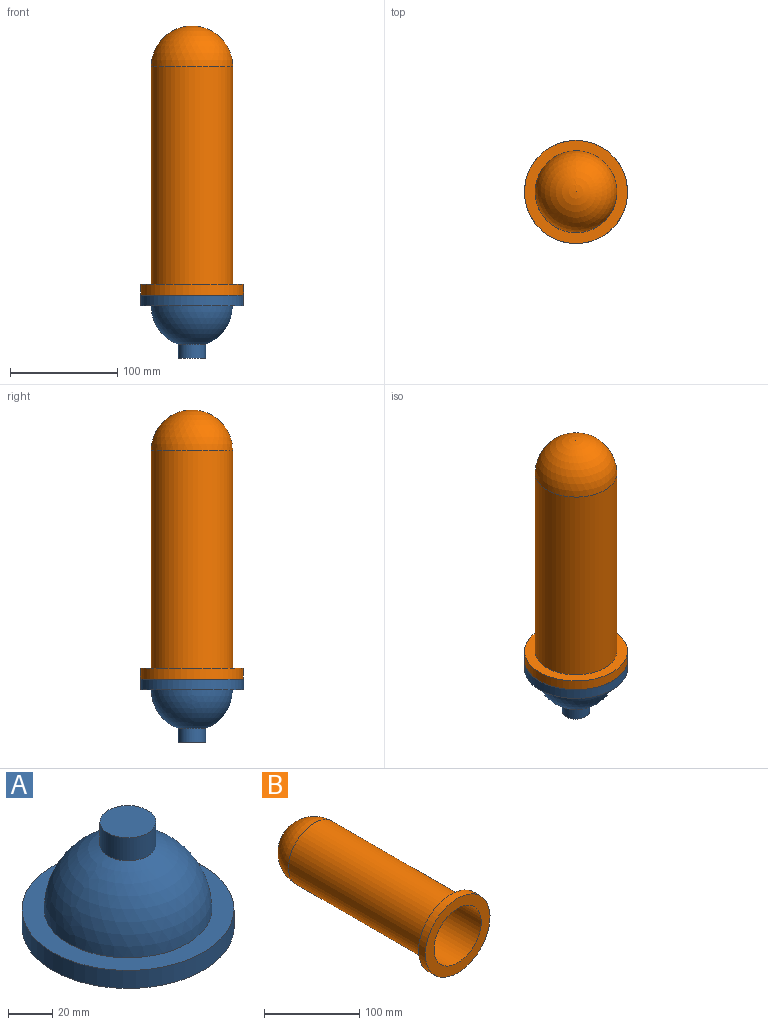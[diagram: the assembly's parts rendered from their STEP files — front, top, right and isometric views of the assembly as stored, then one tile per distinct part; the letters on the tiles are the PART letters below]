
ASSEMBLY  parts=2 mates=1
PART A: 8 faces, bbox 96.2x96.2x58.6 mm
  f0: sphere r=38.1mm, area 8599.1mm2, adj f2,f3
  f1: plane 25.4x25.4mm, normal (0,0,1), area 506.7mm2, adj f2
  f2: cylinder r=12.7mm len=25.4mm, axis (0,0,-1), area 1013.4mm2, adj f0,f1
  f3: plane 96.2x96.2mm, normal (0,0,1), area 2708.1mm2, adj f0,f4
  f4: cylinder r=48.1mm len=96.2mm, axis (0,0,1), area 3022.2mm2, adj f3,f6
  f5: cylinder r=35.1mm len=70.2mm, axis (0,0,1), area 2205.4mm2, adj f6,f7
  f6: plane 96.2x96.2mm, normal (0,0,-1), area 3397.9mm2, adj f4,f5
  f7: sphere r=35.1mm, area 7740.9mm2, adj f5
PART B: 7 faces, bbox 96.2x251.3x96.2 mm
  f0: cylinder r=35.1mm len=213.2mm, axis (0,1,0), area 47019.1mm2, adj f1,f3
  f1: sphere r=35.1mm, area 7740.9mm2, adj f0
  f2: cylinder r=48.1mm len=96.2mm, axis (0,1,0), area 3022.2mm2, adj f3,f4
  f3: plane 96.2x96.2mm, normal (0,-1,0), area 3397.9mm2, adj f0,f2
  f4: plane 96.2x96.2mm, normal (0,1,0), area 2708.1mm2, adj f2,f6
  f5: sphere r=38.1mm, area 9120.7mm2, adj f6
  f6: cylinder r=38.1mm len=203.2mm, axis (0,1,0), area 48643.9mm2, adj f4,f5
PLACE A rot(axis=(-1,0,0),180deg) t=(-0.08,0.18,-126.78)mm
PLACE B rot(axis=(1,0,0),90deg) t=(-0.08,0.18,96.42)mm
MATE fastened A.f5 <-> B.f2  axis (0,0,1) through (-0.08,0.18,-116.78)mm
